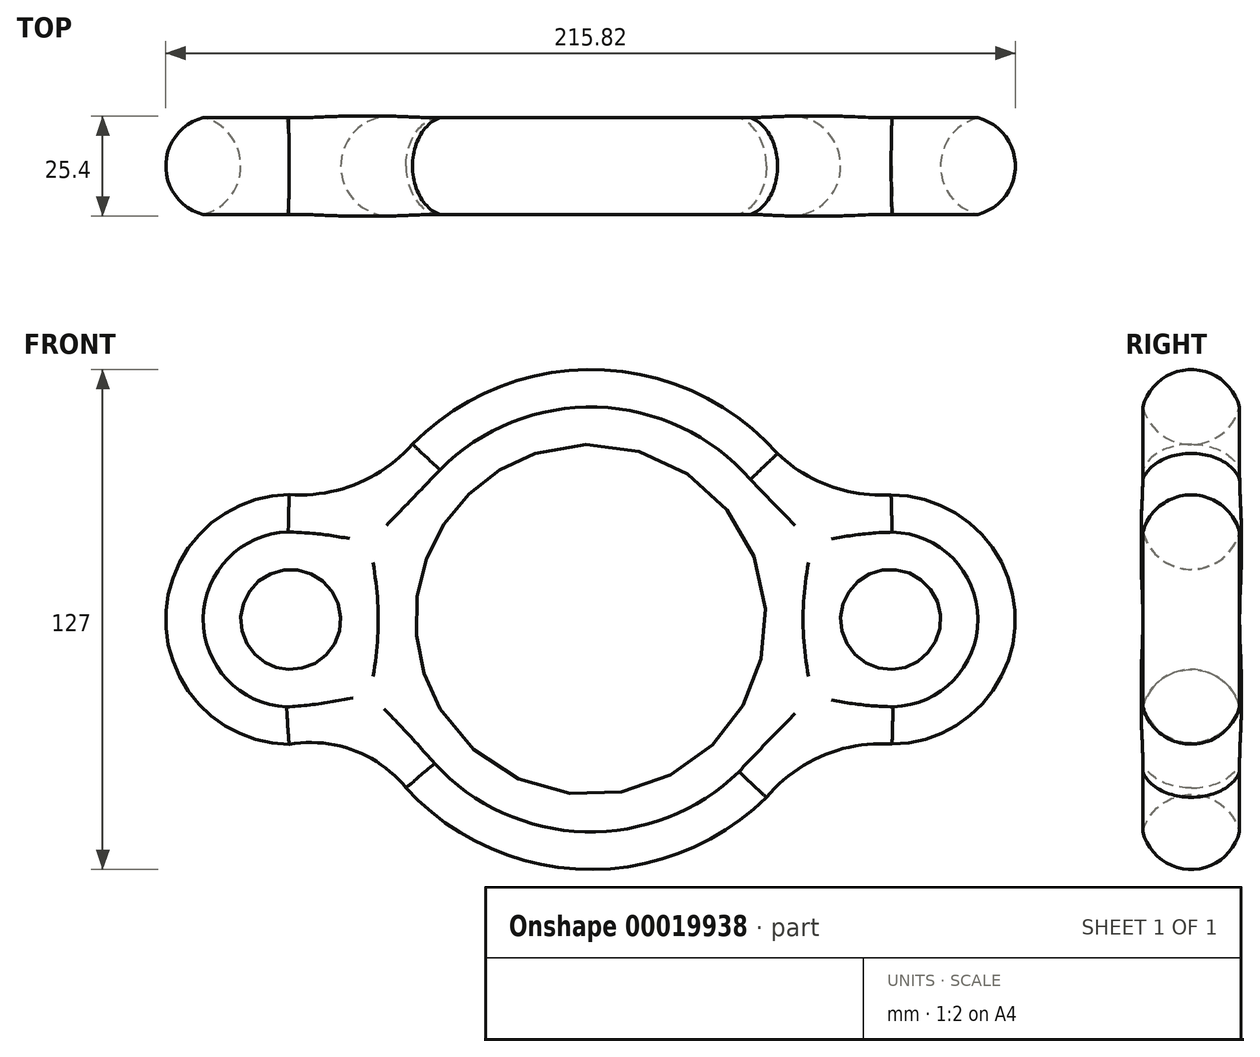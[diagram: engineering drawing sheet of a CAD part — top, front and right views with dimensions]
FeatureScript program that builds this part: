
annotation { "Feature Type Name" : "Feature", "Feature Type Description" : "" }
export const myFeature = defineFeature(function(context is Context, id is Id, definition is map)
    precondition{}
    {
        {
            var Q0;
            Q0=qCreatedBy(makeId("Front.planeOp"),FACE);
            var sketch = newSketch(context, id + "F0", { "sketchPlane" : qUnion([Q0])});
            skCircle(sketch, "E0", {"center": v(0, 0) * mm, "radius": 44.45 * mm});
            skArc(sketch, "E1", {"start": v(-48.56, -40.92) * mm, "mid": v(-0.68, -63.5) * mm, "end": v(47.67, -41.95) * mm});
            skCircle(sketch, "E2", {"center": v(-76.2, 0) * mm, "radius": 12.7 * mm});
            skArc(sketch, "E3", {"start": v(-73.64, 31.65) * mm, "mid": v(-107.91, -1.52) * mm, "end": v(-70.63, -31.26) * mm});
            skCircle(sketch, "E4", {"center": v(76.2, 0) * mm, "radius": 12.7 * mm});
            skArc(sketch, "E5", {"start": v(73.66, -31.57) * mm, "mid": v(107.87, -0.13) * mm, "end": v(73.92, 31.59) * mm});
            skArc(sketch, "E6", {"start": v(-46.9, -42.8) * mm, "mid": v(-60.24, -33.2) * mm, "end": v(-76.6, -31.75) * mm});
            skArc(sketch, "E7", {"start": v(-76.6, 31.75) * mm, "mid": v(-59.44, 34.47) * mm, "end": v(-45.27, 44.53) * mm});
            skArc(sketch, "E8", {"start": v(47.46, 42.19) * mm, "mid": v(60.79, 33.9) * mm, "end": v(76.33, 31.67) * mm});
            skArc(sketch, "E9", {"start": v(76.57, -31.67) * mm, "mid": v(58.97, -34.58) * mm, "end": v(44.62, -45.18) * mm});
            skArc(sketch, "E10.trimOffspring", {"start": v(47.46, 42.19) * mm, "mid": v(0.32, 63.5) * mm, "end": v(-47.03, 42.67) * mm});
            skLineSegment(sketch, "E11", {"start": v(-70.63, -31.26) * mm, "end": v(-70.63, 31.65) * mm});
            skSolve(sketch);
        }
        {
            var Q0;
            Q0=makeQuery(id+"F0.imprint","IMPRINT",FACE,{"disambiguationData":[TD([[makeQuery(id+"F0.imprint","IMPRINT",EDGE,{"derivedFrom":sQuery(id+"F0.wireOp",EDGE,"E0")}),-1.0]])]});
            extrude(context, id + "F1", {"entities" : qUnion([Q0]), "depth" : 25.4 * mm});
        }
        {
            var Q0;
            Q0=makeQuery(id+"F1.opExtrude","CAP_FACE",FACE,{"disambiguationData":[OSD([sQuery(id+"F0.wireOp",EDGE,"E0"),sQuery(id+"F0.wireOp",EDGE,"E1"),sQuery(id+"F0.wireOp",EDGE,"E2"),sQuery(id+"F0.wireOp",EDGE,"E3"),sQuery(id+"F0.wireOp",EDGE,"E4"),sQuery(id+"F0.wireOp",EDGE,"E5"),sQuery(id+"F0.wireOp",EDGE,"E6"),sQuery(id+"F0.wireOp",EDGE,"E7"),sQuery(id+"F0.wireOp",EDGE,"E8"),sQuery(id+"F0.wireOp",EDGE,"E9"),sQuery(id+"F0.wireOp",EDGE,"E10.trimOffspring")])],"isStart":true});
            fillet(context, id + "F2", {"entities" : qUnion([Q0]), "radius" : 12.7 * mm, "tangentPropagation" : true, "allowEdgeOverflow" : false});
        }
        {
            var Q0;
            Q0=makeQuery(id+"F1.opExtrude","CAP_FACE",FACE,{"disambiguationData":[OSD([sQuery(id+"F0.wireOp",EDGE,"E0"),sQuery(id+"F0.wireOp",EDGE,"E1"),sQuery(id+"F0.wireOp",EDGE,"E2"),sQuery(id+"F0.wireOp",EDGE,"E3"),sQuery(id+"F0.wireOp",EDGE,"E4"),sQuery(id+"F0.wireOp",EDGE,"E5"),sQuery(id+"F0.wireOp",EDGE,"E6"),sQuery(id+"F0.wireOp",EDGE,"E7"),sQuery(id+"F0.wireOp",EDGE,"E8"),sQuery(id+"F0.wireOp",EDGE,"E9"),sQuery(id+"F0.wireOp",EDGE,"E10.trimOffspring")])],"isStart":false});
            fillet(context, id + "F3", {"entities" : qUnion([Q0]), "radius" : 12.7 * mm, "tangentPropagation" : true, "allowEdgeOverflow" : false});
        }
    });
